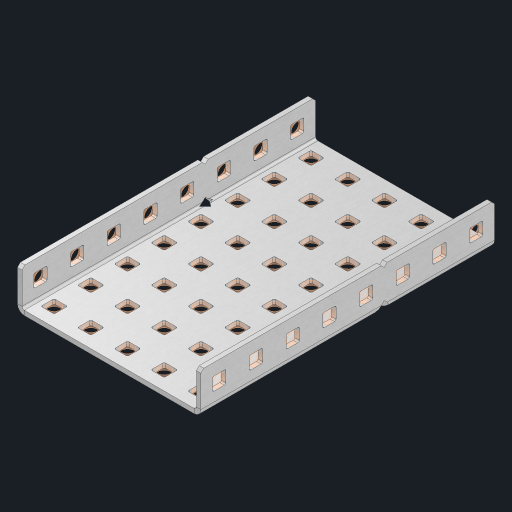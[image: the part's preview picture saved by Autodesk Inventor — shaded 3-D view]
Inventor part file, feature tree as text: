
AUTODESK INVENTOR PART (.ipt)
format: ipt  version: 2023 (Build 270158000, 158)  size: 892,416 bytes
history: native  units: in
note: dims shown in document units (in); Inventor stores cm internally (conversion verified against a paired STEP export)
features: other x61, extrude x55, sheet_metal_op x10, sketch x8, mirror x1, pattern_linear x1, chamfer x1
ambient origin geometry x8: Origin, YZ Plane, XZ Plane, XY Plane, X Axis, Y Axis, Z Axis, Center Point
bodies: Solid1 (feature_tree), Body (feature_tree)
feature tree (137):
  other  "Flange Pattern Plane"
  sheet_metal_op  "Flange Pattern"
  sheet_metal_op  "Body Pattern"
  other  "Arc Length"
  mirror  "Notch Mirror"
  pattern_linear  "Notch Pattern"  Spacing1=0.25in  [1 undecoded]
  chamfer  "End Chamfer"
  extrude  "Half Cut"  Depth=0.0625in
  sketch  "Sketch1"  dims[d0=2.5in]
  other  "Plate1"
  sketch  "Sketch2"  dims[d1=4.0in]
  other  "Plate2"
  sheet_metal_op  "Bend1"
  sheet_metal_op  "Corner1"
  sketch  "Sketch3"  dims[d2=0.0625in]
  other  "Flange Pattern Sketch"
  sketch  "Sketch7"  dims[d3=0.0625in]
  other  "Srf1"
  other  "Srf2"
  sketch  "Sketch8"  dims[d4=0.0312in]
  sketch  "Sketch9"  dims[d5=0.125in]
  other  "Srf91"
  sheet_metal_op  "Body Pattern Sketch"
  other  "Srf92"
  sketch  "Sketch13"  dims[d6=0.0625in]
  sketch  "Sketch14"  dims[d7=0.5in d8=90.0deg d9=0.0312in d10=0.25in d11=0.0625in d12=0.0625in d16=0.182in d17=0.02in d18=0.0625in d19=0.0in d20=0.25in d21=0.25in d46=0.172in d47=1.0in d48=0.0in d49=0.182in d50=0.02in d51=0.25in d52=0.25in d53=0.0625in d54=0.0in d55=0.172in d56=1.0in d57=0.0in d60=3.1496in d62=0.5in d63=1.9685in d65=0.5in d85=0.1473in d86=0.1782in d88=0.04in d89=0.0625in d90=0.0in d91=0.04in d92=0.0491in d95=2.5in d96=0.04in d97=0.25in d98=45.0deg d101=0.0in d102=2.497in d131=2.5in d132=3.1496in d134=0.5in d139=0.5in]
  other  "Srf856"
  other  "Srf1310"
  other  "Srf1311"
  other  "Srf1312"
  other  "Srf1376"
  other  "Srf1377"
  other  "Srf1728"
  other  "Srf1755"
  other  "Srf1878"
  other  "Srf1879"
  other  "Srf1880"
  other  "Srf1881"
  other  "Srf1882"
  other  "Srf1883"
  other  "Srf1884"
  other  "Srf1885"
  other  "Srf1886"
  other  "Srf1887"
  other  "Srf1942"
  other  "Srf1943"
  other  "Srf1944"
  other  "Srf1945"
  other  "Srf1946"
  other  "Srf1947"
  other  "Srf1948"
  other  "Srf1949"
  other  "Srf1950"
  other  "Srf1951"
  other  "Srf1952"
  other  "Srf1953"
  other  "Srf1954"
  other  "Srf1955"
  other  "Srf1956"
  other  "Srf1957"
  other  "Srf1958"
  other  "Srf1959"
  other  "Srf1960"
  other  "Srf1961"
  other  "Srf1962"
  other  "Srf1963"
  other  "Srf1964"
  other  "Srf1965"
  other  "Srf1966"
  other  "Srf1967"
  other  "Srf1968"
  other  "Srf1969"
  other  "Srf1970"
  other  "Srf2146"
  other  "Srf2147"
  other  "Srf2148"
  other  "Srf2149"
  other  "Srf2150"
  sheet_metal_op  "Flange Stamp"
  sheet_metal_op  "Flange Circle"
  sheet_metal_op  "Body Stamp"
  sheet_metal_op  "Body Circle"
  sheet_metal_op  "Notch"
  extrude  "ExtrusionSrf2"  Depth=0.0625in
  extrude  "ExtrusionSrf92"  Depth=2.5in
  extrude  "ExtrusionSrf856"  Depth=0.02in
  extrude  "ExtrusionSrf1310"  Depth=0.0625in
  extrude  "ExtrusionSrf1311"  TaperAngle=0.0deg  [1 undecoded]
  extrude  "ExtrusionSrf1312"  Depth=0.25in
  extrude  "ExtrusionSrf1376"  Depth=0.25in
  extrude  "ExtrusionSrf1377"  Depth=2.5in
  extrude  "ExtrusionSrf1728"  Depth=2.5in TaperAngle=0.0deg
  extrude  "ExtrusionSrf1755"  Depth=2.5in
  extrude  "ExtrusionSrf1878"  Depth=0.02in
  extrude  "ExtrusionSrf1879"  Depth=0.25in
  extrude  "ExtrusionSrf1880"  Depth=0.25in
  extrude  "ExtrusionSrf1881"  Depth=0.0625in
  extrude  "ExtrusionSrf1882"  TaperAngle=0.0deg  [1 undecoded]
  extrude  "ExtrusionSrf1883"  Depth=2.5in
  extrude  "ExtrusionSrf1884"  Depth=2.5in TaperAngle=0.0deg
  extrude  "ExtrusionSrf1885"  Depth=2.5in
  extrude  "ExtrusionSrf1886"  Depth=2.5in
  extrude  "ExtrusionSrf1887"  Depth=2.5in
  extrude  "ExtrusionSrf1942"  Depth=2.5in
  extrude  "ExtrusionSrf1943"  Depth=2.5in
  extrude  "ExtrusionSrf1944"  Depth=0.0625in
  extrude  "ExtrusionSrf1945"  TaperAngle=0.0deg  [1 undecoded]
  extrude  "ExtrusionSrf1946"  Depth=2.5in
  extrude  "ExtrusionSrf1947"  Depth=2.5in
  extrude  "ExtrusionSrf1948"  Depth=2.5in
  extrude  "ExtrusionSrf1949"  Depth=0.25in TaperAngle=45.0deg
  extrude  "ExtrusionSrf1950"  TaperAngle=0.0deg  [1 undecoded]
  extrude  "ExtrusionSrf1951"  Depth=2.5in
  extrude  "ExtrusionSrf1952"  Depth=2.5in
  extrude  "ExtrusionSrf1953"  Depth=2.5in
  extrude  "ExtrusionSrf1954"  Depth=2.5in
  extrude  "ExtrusionSrf1955"  Depth=2.5in
  extrude  "ExtrusionSrf1956"  [1 undecoded]
  extrude  "ExtrusionSrf1957"  [1 undecoded]
  extrude  "ExtrusionSrf1958"  [1 undecoded]
  extrude  "ExtrusionSrf1959"  [1 undecoded]
  extrude  "ExtrusionSrf1960"  [1 undecoded]
  extrude  "ExtrusionSrf1961"  [1 undecoded]
  extrude  "ExtrusionSrf1962"  [1 undecoded]
  extrude  "ExtrusionSrf1963"  [1 undecoded]
  extrude  "ExtrusionSrf1964"  [1 undecoded]
  extrude  "ExtrusionSrf1965"  [1 undecoded]
  extrude  "ExtrusionSrf1966"  [1 undecoded]
  extrude  "ExtrusionSrf1967"  [1 undecoded]
  extrude  "ExtrusionSrf1968"  [1 undecoded]
  extrude  "ExtrusionSrf1969"  [1 undecoded]
  extrude  "ExtrusionSrf1970"  [1 undecoded]
  extrude  "ExtrusionSrf2146"  [1 undecoded]
  extrude  "ExtrusionSrf2147"  [1 undecoded]
  extrude  "ExtrusionSrf2148"  [1 undecoded]
  extrude  "ExtrusionSrf2149"  [1 undecoded]
  extrude  "ExtrusionSrf2150"  [1 undecoded]
note: 25 required parameter values undecoded (feature->parameter linkage not recoverable at this tier; creation-order binding heuristic only, values carry confidence <= 0.55)
